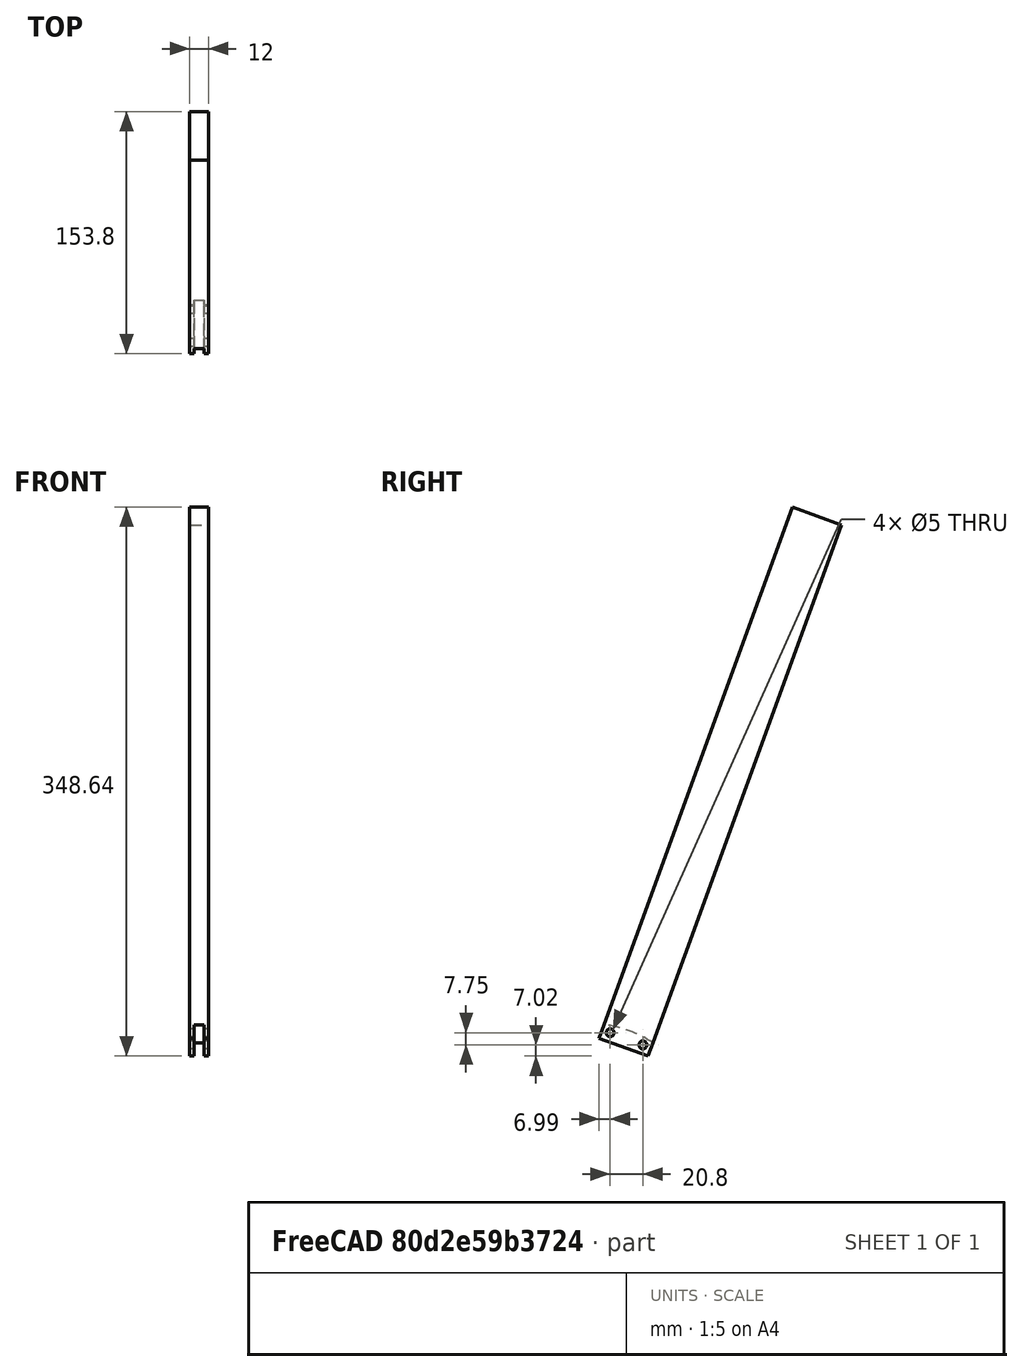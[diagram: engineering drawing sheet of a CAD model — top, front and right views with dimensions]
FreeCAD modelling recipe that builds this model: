
FCSTD DOCUMENT  (FreeCAD 0.18R16110 (Git))
Label: longarm
License: All rights reserved
LicenseURL: http://en.wikipedia.org/wiki/All_rights_reserved
objects: Part::Cylinder×3, Part::Cut×3, Sketcher::SketchObject×1, Part::Extrusion×1, Mesh::Feature×1
note: 8 computed .brp shape members not serialized (recipe doc carries the construction recipe); baked Part::Feature solids carry a one-line shape summary decoded from their .brp

FEATURE [Sketcher::SketchObject] Sketch
  sketch-geometry (6):
    g0: LineSegment StartX=-6 StartY=0 StartZ=0 EndX=6 EndY=5e-16 EndZ=0
    g1: LineSegment StartX=6 StartY=5e-16 StartZ=0 EndX=6 EndY=9 EndZ=0
    g2: LineSegment StartX=-6 StartY=359 StartZ=0 EndX=-6 EndY=9 EndZ=0
    g3: LineSegment StartX=-6 StartY=9 StartZ=0 EndX=-6 EndY=0 EndZ=0
    g4: LineSegment StartX=-6 StartY=359 StartZ=0 EndX=6 EndY=359 EndZ=0
    g5: LineSegment StartX=6 StartY=359 StartZ=0 EndX=6 EndY=9 EndZ=0
  constraints (16):
    c: PointOnObject(g0,g-1)
    c: Coincident(g0,g1)
    c: Vertical(g1)
    c: Coincident(g2,g3)
    c: Coincident(g3,g0)
    c: Symmetric(g0,g0,g-2)
    c: Symmetric(g2,g1,g-2)
    c: DistanceX(g0,g0) = 12
    c: DistanceY(g3,g3) = 9
    c: DistanceX(g2) = -6
    c: Distance(g2) = 350
    c: Coincident(g2,g4)
    c: Coincident(g4,g5)
    c: Coincident(g5,g1)
    c: Vertical(g5)
    c: Horizontal(g4)
FEATURE [Part::Extrusion] Extrude
  Base = -> Sketch
  Dir = (0,0,1)
  DirMode = 2
  FaceMakerClass = Part::FaceMakerBullseye
  LengthFwd = 33
  LengthRev = 0
  Solid = true
  Symmetric = false
FEATURE [Part::Cylinder] Cylinder
  Angle = 360
  AttacherType = Attacher::AttachEngine3D
  Height = 6.1
  Placement = pos=(-3,-59,17) rot=(0,1,0;1.5708rad)
  Radius = 70
FEATURE [Part::Cut] Cut
  Base = -> Extrude
  Placement = pos=(0,36.22,49.58) rot=(1,0,0;1.22173rad)
  Tool = -> Cylinder
FEATURE [Part::Cylinder] Cylinder001
  Angle = 360
  AttacherType = Attacher::AttachEngine3D
  Height = 15
  Placement = pos=(7.5,33,56.6) rot=(0,-1,0;1.5708rad)
  Radius = 2.5
FEATURE [Part::Cylinder] Cylinder002
  Angle = 360
  AttacherType = Attacher::AttachEngine3D
  Height = 15
  Placement = pos=(7.5,12.2,64.35) rot=(0,-1,0;1.5708rad)
  Radius = 2.5
FEATURE [Part::Cut] Cut001
  Base = -> Cut
  Tool = -> Cylinder001
FEATURE [Part::Cut] Cut002
  Base = -> Cut001
  Tool = -> Cylinder002
FEATURE [Mesh::Feature] armscrew
  Placement = pos=(0,70.25,189.4) rot=(0,0,1;0rad)
